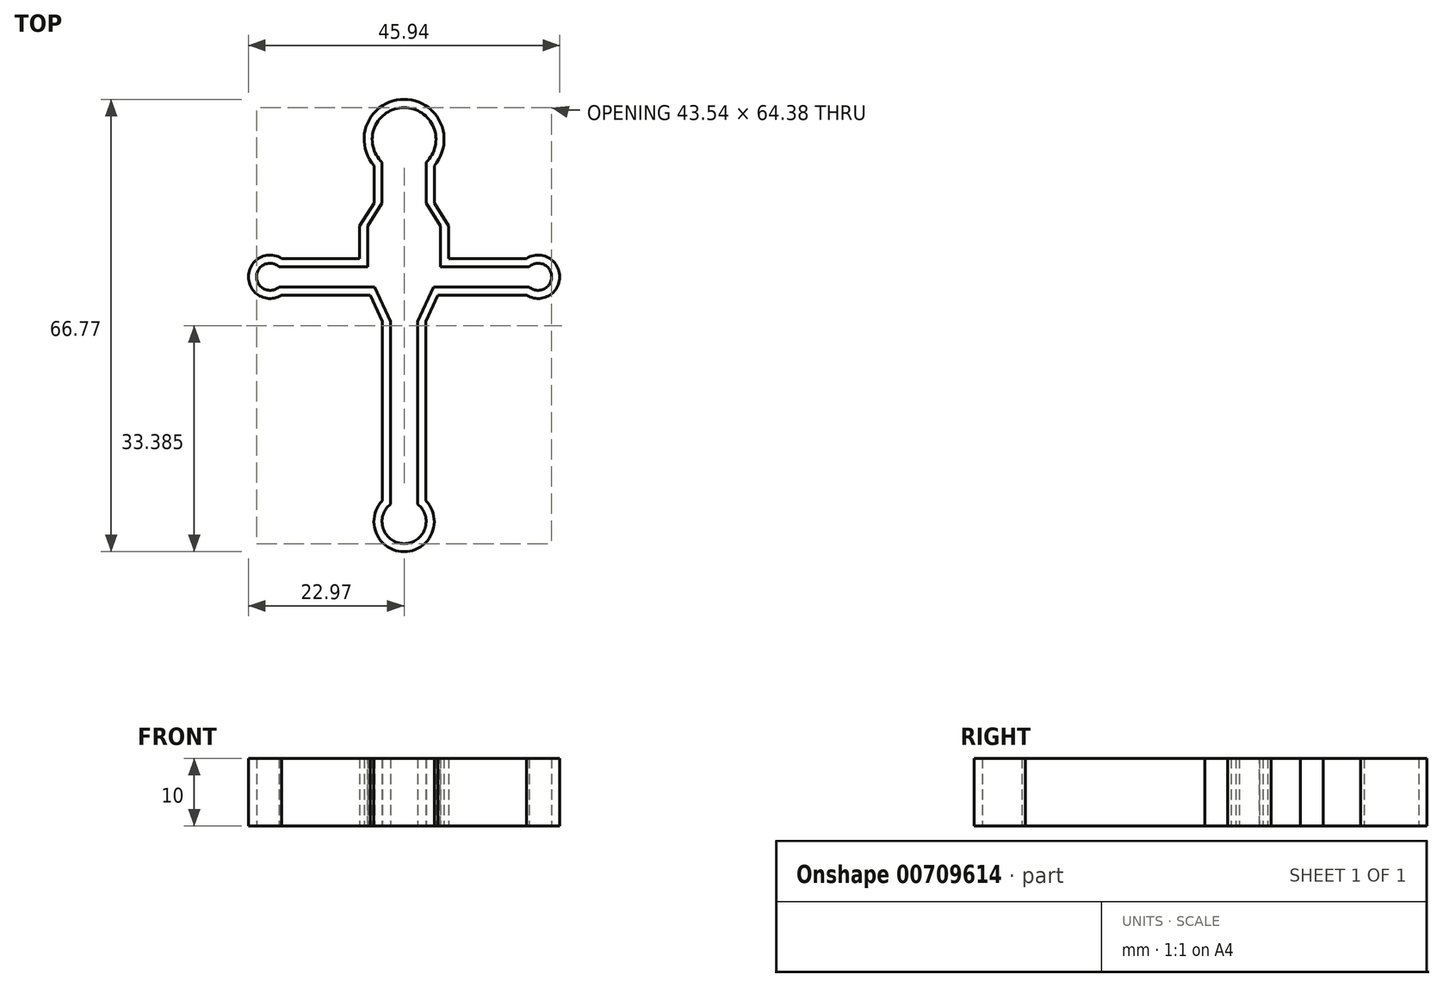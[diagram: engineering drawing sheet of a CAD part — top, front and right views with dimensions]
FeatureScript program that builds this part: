
annotation { "Feature Type Name" : "Feature", "Feature Type Description" : "" }
export const myFeature = defineFeature(function(context is Context, id is Id, definition is map)
    precondition{}
    {
        {
            var Q0;
            Q0=qCreatedBy(makeId("Top.planeOp"),FACE);
            var sketch = newSketch(context, id + "F0", { "sketchPlane" : qUnion([Q0])});
            skLineSegment(sketch, "E0", {"start": v(5.37, -0.5) * mm, "end": v(18.45, -0.5) * mm});
            skLineSegment(sketch, "E1", {"start": v(5.37, -0.5) * mm, "end": v(5.37, 5.5) * mm});
            skLineSegment(sketch, "E2.MirrorCS", {"start": v(-115.65, -62.32) * mm, "end": v(-115.65, -62.32) * mm});
            skLineSegment(sketch, "E3", {"start": v(2, -8.57) * mm, "end": v(2, -35.57) * mm});
            skLineSegment(sketch, "E4", {"start": v(3.25, 8.9) * mm, "end": v(3.25, 14.9) * mm});
            skLineSegment(sketch, "E5", {"start": v(4.37, -3.5) * mm, "end": v(2, -8.57) * mm});
            skLineSegment(sketch, "E6", {"start": v(5.37, 5.5) * mm, "end": v(3.25, 8.9) * mm});
            skArc(sketch, "E7", {"start": v(0, -41.38) * mm, "mid": v(3.07, -39.2) * mm, "end": v(2, -35.57) * mm});
            skArc(sketch, "E8", {"start": v(3.25, 14.9) * mm, "mid": v(4.36, 20.04) * mm, "end": v(0, 23) * mm});
            skArc(sketch, "E9", {"start": v(18.45, -3.5) * mm, "mid": v(21.77, -2) * mm, "end": v(18.45, -0.5) * mm});
            skLineSegment(sketch, "E10.trimOffspring", {"start": v(18.45, -3.5) * mm, "end": v(4.37, -3.5) * mm});
            skLineSegment(sketch, "E11", {"start": v(6.57, 0.7) * mm, "end": v(18.05, 0.7) * mm});
            skLineSegment(sketch, "E12", {"start": v(3.2, -8.57) * mm, "end": v(3.2, -35.04) * mm});
            skLineSegment(sketch, "E13", {"start": v(5, -4.7) * mm, "end": v(3.2, -8.57) * mm});
            skArc(sketch, "E14", {"start": v(18.05, -4.7) * mm, "mid": v(22.97, -2) * mm, "end": v(18.05, 0.7) * mm});
            skArc(sketch, "E15", {"start": v(0, -42.58) * mm, "mid": v(4.1, -39.87) * mm, "end": v(3.2, -35.04) * mm});
            skPoint(sketch, "E16.orphan", {"position": v(3.2, -35.57) * mm});
            skPoint(sketch, "E17.start.orphan", {"position": v(3.25, 11.9) * mm});
            skLineSegment(sketch, "E18", {"start": v(4.45, 8.9) * mm, "end": v(6.57, 5.5) * mm});
            skLineSegment(sketch, "E19", {"start": v(6.57, 5.5) * mm, "end": v(6.57, 0.7) * mm});
            skLineSegment(sketch, "E20", {"start": v(4.45, 8.9) * mm, "end": v(4.45, 14.42) * mm});
            skArc(sketch, "E21", {"start": v(4.45, 14.42) * mm, "mid": v(5.37, 20.74) * mm, "end": v(0, 24.2) * mm});
            skLineSegment(sketch, "E22", {"start": v(5, -4.7) * mm, "end": v(18.05, -4.7) * mm});
            skLineSegment(sketch, "E23.MirrorCS", {"start": v(-4.45, 8.9) * mm, "end": v(-6.57, 5.5) * mm});
            skLineSegment(sketch, "E24.MirrorCS", {"start": v(-5.37, 5.5) * mm, "end": v(-3.25, 8.9) * mm});
            skLineSegment(sketch, "E25.MirrorCS", {"start": v(-4.45, 8.9) * mm, "end": v(-4.45, 14.42) * mm});
            skLineSegment(sketch, "E26.MirrorCS", {"start": v(-3.25, 8.9) * mm, "end": v(-3.25, 14.9) * mm});
            skLineSegment(sketch, "E27.MirrorCS", {"start": v(-6.57, 5.5) * mm, "end": v(-6.57, 0.7) * mm});
            skArc(sketch, "E28.MirrorCS", {"start": v(-4.45, 14.42) * mm, "mid": v(-5.37, 20.74) * mm, "end": v(0, 24.2) * mm});
            skArc(sketch, "E29.MirrorCS", {"start": v(-3.25, 14.9) * mm, "mid": v(-4.36, 20.04) * mm, "end": v(0, 23) * mm});
            skLineSegment(sketch, "E30.MirrorCS", {"start": v(-5.37, -0.5) * mm, "end": v(-5.37, 5.5) * mm});
            skLineSegment(sketch, "E31.MirrorCS", {"start": v(-18.45, -3.5) * mm, "end": v(-4.37, -3.5) * mm});
            skArc(sketch, "E32.MirrorCS", {"start": v(0, -41.38) * mm, "mid": v(-3.07, -39.2) * mm, "end": v(-2, -35.57) * mm});
            skLineSegment(sketch, "E33.MirrorCS", {"start": v(-4.37, -3.5) * mm, "end": v(-2, -8.57) * mm});
            skLineSegment(sketch, "E34.MirrorCS", {"start": v(-6.57, 0.7) * mm, "end": v(-18.05, 0.7) * mm});
            skLineSegment(sketch, "E35.MirrorCS", {"start": v(-3.2, -8.57) * mm, "end": v(-3.2, -35.04) * mm});
            skLineSegment(sketch, "E36.MirrorCS", {"start": v(-2, -8.57) * mm, "end": v(-2, -35.57) * mm});
            skPoint(sketch, "E37.MirrorP", {"position": v(-3.2, -35.57) * mm});
            skLineSegment(sketch, "E38.MirrorCS", {"start": v(-5, -4.7) * mm, "end": v(-3.2, -8.57) * mm});
            skLineSegment(sketch, "E39.MirrorCS", {"start": v(-5.37, -0.5) * mm, "end": v(-18.45, -0.5) * mm});
            skLineSegment(sketch, "E40.MirrorCS", {"start": v(-5, -4.7) * mm, "end": v(-18.05, -4.7) * mm});
            skArc(sketch, "E41.MirrorCS", {"start": v(-18.45, -3.5) * mm, "mid": v(-21.77, -2) * mm, "end": v(-18.45, -0.5) * mm});
            skArc(sketch, "E42.MirrorCS", {"start": v(-18.05, -4.7) * mm, "mid": v(-22.97, -2) * mm, "end": v(-18.05, 0.7) * mm});
            skPoint(sketch, "E43.MirrorP", {"position": v(-3.25, 11.9) * mm});
            skArc(sketch, "E44.MirrorCS", {"start": v(0, -42.58) * mm, "mid": v(-4.1, -39.87) * mm, "end": v(-3.2, -35.04) * mm});
            skSolve(sketch);
        }
        {
            var Q0;
            Q0=makeQuery(id+"F0.imprint","IMPRINT",FACE,{"disambiguationData":[TD([[makeQuery(id+"F0.imprint","IMPRINT",EDGE,{"derivedFrom":sQuery(id+"F0.wireOp",EDGE,"E0")}),1.0]])]});
            var Q1;
            Q1=makeQuery(id+"F0.imprint","IMPRINT",FACE,{"disambiguationData":[TD([[makeQuery(id+"F0.imprint","IMPRINT",EDGE,{"derivedFrom":sQuery(id+"F0.wireOp",EDGE,"2c8baa50-92ca-49bf-a817-a55542107715.MirrorCS")}),-1.0]])]});
            extrude(context, id + "F1", {"entities" : qUnion([Q0, Q1]), "depth" : 10 * mm, "offsetDistance" : 25 * mm});
        }
    });
